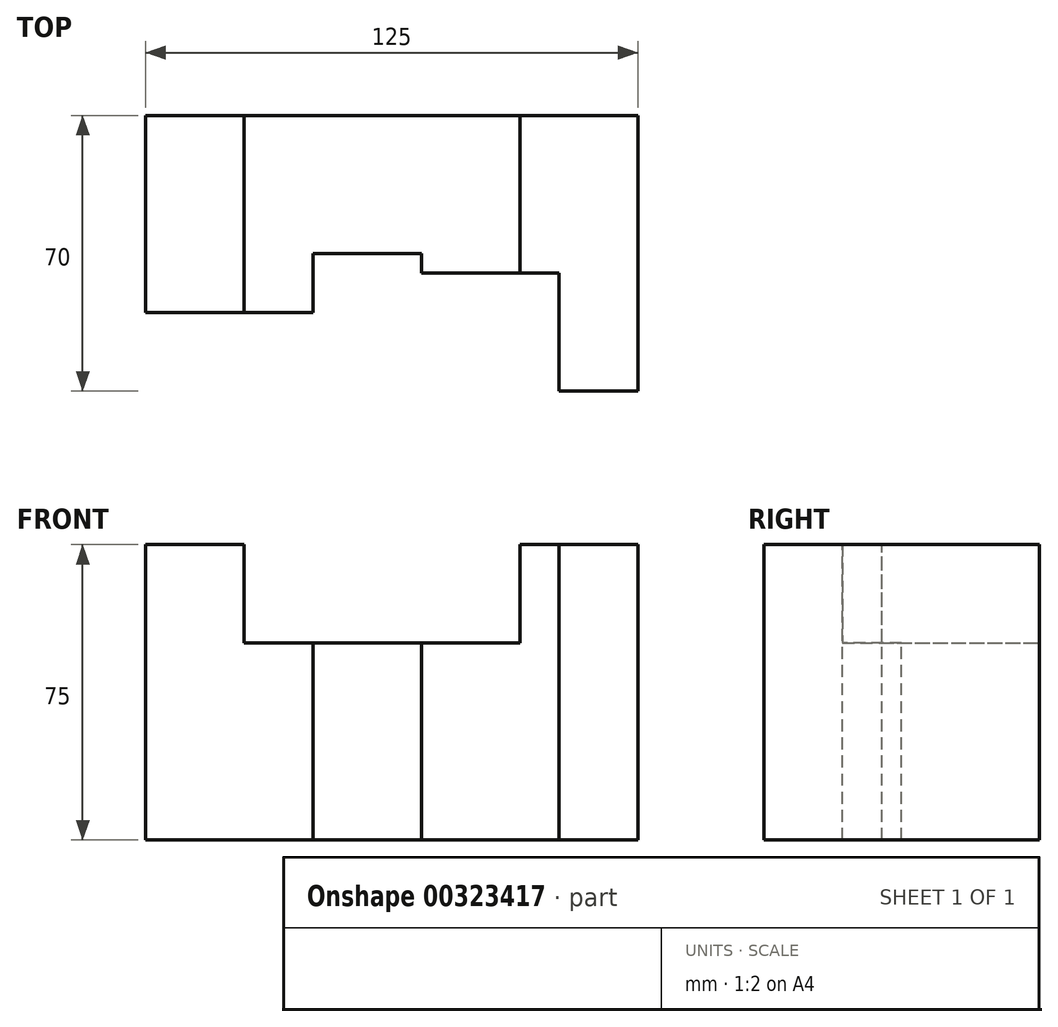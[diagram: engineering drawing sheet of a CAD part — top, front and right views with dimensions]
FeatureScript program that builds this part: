
annotation { "Feature Type Name" : "Feature", "Feature Type Description" : "" }
export const myFeature = defineFeature(function(context is Context, id is Id, definition is map)
    precondition{}
    {
        {
            var Q0;
            Q0=qCreatedBy(makeId("Front.planeOp"),FACE);
            var sketch = newSketch(context, id + "F0", { "sketchPlane" : qUnion([Q0])});
            skLineSegment(sketch, "E0", {"start": v(0, 0) * mm, "end": v(0, 75) * mm});
            skLineSegment(sketch, "E1", {"start": v(0, 75) * mm, "end": v(25, 75) * mm});
            skLineSegment(sketch, "E2", {"start": v(25, 75) * mm, "end": v(25, 50) * mm});
            skLineSegment(sketch, "E3", {"start": v(25, 50) * mm, "end": v(95, 50) * mm});
            skLineSegment(sketch, "E4", {"start": v(95, 50) * mm, "end": v(95, 75) * mm});
            skLineSegment(sketch, "E5", {"start": v(95, 75) * mm, "end": v(125, 75) * mm});
            skLineSegment(sketch, "E6", {"start": v(125, 75) * mm, "end": v(125, 0) * mm});
            skLineSegment(sketch, "E7", {"start": v(125, 0) * mm, "end": v(0, 0) * mm});
            skLineSegment(sketch, "E8", {"start": v(42.5, 50) * mm, "end": v(42.5, 0) * mm});
            skLineSegment(sketch, "E9", {"start": v(70, 50) * mm, "end": v(70, 0) * mm});
            skLineSegment(sketch, "E10", {"start": v(105, 75) * mm, "end": v(105, 0) * mm});
            skSolve(sketch);
        }
        {
            var Q0;
            {var subQ4=sQuery(id+"F0.wireOp",EDGE,"E0");Q0=makeQuery(id+"F0.imprint","IMPRINT",FACE,{"disambiguationData":[TD([[makeQuery(id+"F0.imprint","IMPRINT",EDGE,{"derivedFrom":subQ4}),-1.0]])]});}
            var Q1;
            {var subQ0=sQuery(id+"F0.wireOp",EDGE,"E6");Q1=makeQuery(id+"F0.imprint","IMPRINT",FACE,{"disambiguationData":[TD([[makeQuery(id+"F0.imprint","IMPRINT",EDGE,{"derivedFrom":subQ0}),-1.0]])]});}
            var Q2;
            {var subQ0=sQuery(id+"F0.wireOp",EDGE,"E8");Q2=makeQuery(id+"F0.imprint","IMPRINT",FACE,{"disambiguationData":[TD([[makeQuery(id+"F0.imprint","IMPRINT",EDGE,{"derivedFrom":subQ0}),1.0]])]});}
            var Q3;
            {var subQ1=sQuery(id+"F0.wireOp",EDGE,"E4");Q3=makeQuery(id+"F0.imprint","IMPRINT",FACE,{"disambiguationData":[TD([[makeQuery(id+"F0.imprint","IMPRINT",EDGE,{"derivedFrom":subQ1}),-1.0]])]});}
            extrude(context, id + "F1", {"entities" : qUnion([Q0, Q1, Q2, Q3]), "depth" : 50 * mm, "symmetric" : true});
        }
        {
            var Q0;
            Q0=makeQuery(id+"F1.opExtrude","SWEPT_FACE",FACE,{"disambiguationData":[OSD([sQuery(id+"F0.wireOp",EDGE,"E3")])]});
            var sketch = newSketch(context, id + "F2", { "sketchPlane" : qUnion([Q0])});
            skPoint(sketch, "E11.0", {"position": v(42.5, 0) * mm});
            skPoint(sketch, "E12.0", {"position": v(70, 0) * mm});
            skPoint(sketch, "E13.0", {"position": v(105, 0) * mm});
            skPoint(sketch, "E13.1", {"position": v(95, 0) * mm});
            skLineSegment(sketch, "E14", {"start": v(42.5, -10) * mm, "end": v(42.5, -25) * mm});
            skLineSegment(sketch, "E15", {"start": v(42.5, -10) * mm, "end": v(70, -10) * mm});
            skLineSegment(sketch, "E16", {"start": v(70, -10) * mm, "end": v(70, -15) * mm});
            skLineSegment(sketch, "E17", {"start": v(70, -15) * mm, "end": v(95, -15) * mm});
            skSolve(sketch);
        }
        {
            var Q0;
            {var subQ1=sQuery(id+"F2.wireOp",EDGE,"E14");Q0=makeQuery(id+"F2.imprint","IMPRINT",FACE,{"disambiguationData":[TD([[makeQuery(id+"F2.imprint","IMPRINT",EDGE,{"derivedFrom":subQ1}),1.0]])]});}
            extrude(context, id + "F3", {"entities" : qUnion([Q0]), "operationType" : NewBodyOperationType.REMOVE, "endBound" : BoundingType.THROUGH_ALL, "oppositeDirection" : true, "depth" : 25 * mm});
        }
        {
            var Q0;
            {var subQ0=sQuery(id+"F0.wireOp",EDGE,"E7");var subQ1=sQuery(id+"F0.wireOp",EDGE,"E6");var subQ2=sQuery(id+"F0.wireOp",EDGE,"E5");var subQ3=sQuery(id+"F0.wireOp",EDGE,"E4");var subQ4=sQuery(id+"F0.wireOp",EDGE,"E3");Q0=makeQuery(id+"F3.boolean.opBoolean","SPLIT",FACE,{"disambiguationData":[TD([makeQuery(id+"F1.opExtrude","SWEPT_FACE",FACE,{"disambiguationData":[OSD([subQ3])]})])],"derivedFrom":makeQuery(id+"F1.opExtrude","CAP_FACE",FACE,{"disambiguationData":[OSD([sQuery(id+"F0.wireOp",EDGE,"E0"),sQuery(id+"F0.wireOp",EDGE,"E1"),sQuery(id+"F0.wireOp",EDGE,"E2"),subQ4,subQ3,subQ2,subQ1,subQ0])],"isStart":false})});}
            extrude(context, id + "F4", {"entities" : qUnion([Q0]), "operationType" : NewBodyOperationType.ADD, "depth" : 20 * mm});
        }
        {
            var Q0;
            {var subQ0=sQuery(id+"F0.wireOp",EDGE,"E5");Q0=makeQuery(id+"F4.boolean.opBoolean","MERGE",FACE,{"derivedFrom":[makeQuery(id+"F1.opExtrude","SWEPT_FACE",FACE,{"disambiguationData":[OSD([subQ0])]}),makeQuery(id+"F4.opExtrude","SWEPT_FACE",FACE,{"disambiguationData":[OSD([subQ0])]})]});}
            var sketch = newSketch(context, id + "F5", { "sketchPlane" : qUnion([Q0])});
            skPoint(sketch, "E18.0", {"position": v(105, 0) * mm});
            skPoint(sketch, "E19.0", {"position": v(95, 0) * mm});
            skLineSegment(sketch, "E20", {"start": v(105, -45) * mm, "end": v(105, -15) * mm});
            skLineSegment(sketch, "E21", {"start": v(105, -15) * mm, "end": v(95, -15) * mm});
            skSolve(sketch);
        }
        {
            var Q0;
            {var subQ0=sQuery(id+"F5.wireOp",EDGE,"E20");Q0=makeQuery(id+"F5.imprint","IMPRINT",FACE,{"disambiguationData":[TD([[makeQuery(id+"F5.imprint","IMPRINT",EDGE,{"derivedFrom":subQ0}),1.0]])]});}
            extrude(context, id + "F6", {"entities" : qUnion([Q0]), "operationType" : NewBodyOperationType.REMOVE, "endBound" : BoundingType.THROUGH_ALL, "oppositeDirection" : true, "depth" : 25 * mm});
        }
    });
